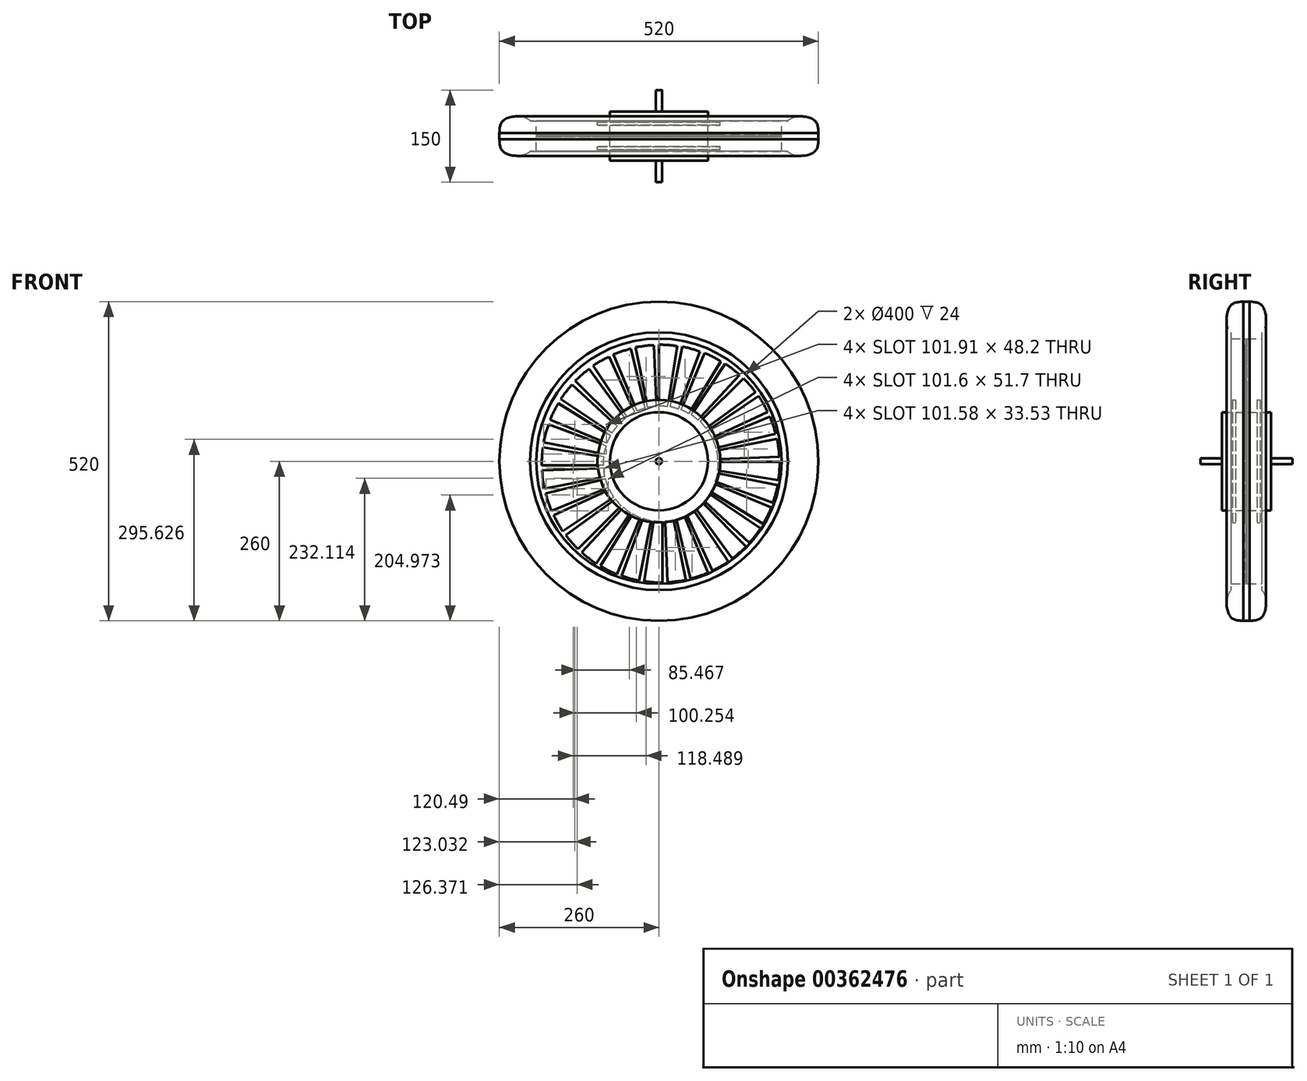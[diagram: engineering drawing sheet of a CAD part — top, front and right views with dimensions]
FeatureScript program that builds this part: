
annotation { "Feature Type Name" : "Feature", "Feature Type Description" : "" }
export const myFeature = defineFeature(function(context is Context, id is Id, definition is map)
    precondition{}
    {
        {
            var Q0;
            Q0=qCreatedBy(makeId("Right.planeOp"),FACE);
            var sketch = newSketch(context, id + "F0", { "sketchPlane" : qUnion([Q0])});
            skLineSegment(sketch, "E0", {"start": v(0, 0) * mm, "end": v(0, 200) * mm, "construction": true});
            skPoint(sketch, "E1.middle", {"position": v(0, 200) * mm});
            skPoint(sketch, "E2.visualSharp", {"position": v(-30.2, 260) * mm});
            skLineSegment(sketch, "E3.left", {"start": v(-1, 200) * mm, "end": v(-1, 80) * mm});
            skLineSegment(sketch, "E4.trimOffspring", {"start": v(-1, 200) * mm, "end": v(-25, 200) * mm});
            skLineSegment(sketch, "E5", {"start": v(-25, 200) * mm, "end": v(-25, 210) * mm});
            skFitSpline(sketch, "E6", {"points": [v(-5, 260) * mm, v(-25.83, 253.38) * mm, v(-32.03, 227.8) * mm, v(-25, 210) * mm], "startDerivative": vector(-86.17, -1.88) * mm, "endDerivative": vector(37.49, -43.12) * mm});
            skLineSegment(sketch, "E7", {"start": v(0, 260) * mm, "end": v(-5, 260) * mm});
            skLineSegment(sketch, "E8", {"start": v(0, 0) * mm, "end": v(-40, 0) * mm});
            skLineSegment(sketch, "E9", {"start": v(-40, 0) * mm, "end": v(-40, 80) * mm});
            skLineSegment(sketch, "E10", {"start": v(-40, 80) * mm, "end": v(-22.5, 80) * mm});
            skLineSegment(sketch, "E11", {"start": v(-22.5, 80) * mm, "end": v(-22.5, 100) * mm});
            skLineSegment(sketch, "E12", {"start": v(-22.5, 100) * mm, "end": v(-17.5, 100) * mm});
            skLineSegment(sketch, "E13", {"start": v(-17.5, 100) * mm, "end": v(-17.5, 80) * mm});
            skLineSegment(sketch, "E14", {"start": v(-17.5, 80) * mm, "end": v(-1, 80) * mm});
            skLineSegment(sketch, "E15.MirrorCS", {"start": v(0, 260) * mm, "end": v(5, 260) * mm});
            skLineSegment(sketch, "E16.MirrorCS", {"start": v(22.5, 100) * mm, "end": v(17.5, 100) * mm});
            skLineSegment(sketch, "E17.MirrorCS", {"start": v(25, 200) * mm, "end": v(25, 210) * mm});
            skLineSegment(sketch, "E18.MirrorCS", {"start": v(1, 200) * mm, "end": v(1, 80) * mm});
            skLineSegment(sketch, "E19.MirrorCS", {"start": v(1, 200) * mm, "end": v(25, 200) * mm});
            skLineSegment(sketch, "E20.MirrorCS", {"start": v(22.5, 80) * mm, "end": v(22.5, 100) * mm});
            skLineSegment(sketch, "E21.MirrorCS", {"start": v(17.5, 100) * mm, "end": v(17.5, 80) * mm});
            skFitSpline(sketch, "E22.MirrorCS", {"points": [v(5, 260) * mm, v(25.83, 253.38) * mm, v(32.03, 227.8) * mm, v(25, 210) * mm], "startDerivative": vector(86.17, -1.88) * mm, "endDerivative": vector(-37.49, -43.12) * mm});
            skLineSegment(sketch, "E23.MirrorCS", {"start": v(40, 80) * mm, "end": v(22.5, 80) * mm});
            skLineSegment(sketch, "E24.MirrorCS", {"start": v(40, 0) * mm, "end": v(40, 80) * mm});
            skLineSegment(sketch, "E25.MirrorCS", {"start": v(0, 0) * mm, "end": v(40, 0) * mm});
            skLineSegment(sketch, "E26.MirrorCS", {"start": v(17.5, 80) * mm, "end": v(1, 80) * mm});
            skPoint(sketch, "E27.MirrorP", {"position": v(30.2, 260) * mm});
            skSolve(sketch);
        }
        {
            var Q0;
            Q0=makeQuery(id+"F0.imprint","IMPRINT",FACE,{"disambiguationData":[TD([[makeQuery(id+"F0.imprint","IMPRINT",EDGE,{"derivedFrom":sQuery(id+"F0.wireOp",EDGE,"E3.left")}),1.0]])]});
            var Q1;
            Q1=sQuery(id+"F0.wireOp",EDGE,"E8");
            revolve(context, id + "F1", {"entities" : qUnion([Q0]), "axis" : qUnion([Q1]), "revolveType" : RevolveType.FULL});
        }
        {
            var Q0;
            Q0=makeQuery(id+"F1.opRevolve","SWEPT_FACE",FACE,{"disambiguationData":[OSD([sQuery(id+"F0.wireOp",EDGE,"E3.left")])]});
            var sketch = newSketch(context, id + "F2", { "sketchPlane" : qUnion([Q0])});
            skLineSegment(sketch, "E28", {"start": v(0, 90) * mm, "end": v(0, 190) * mm});
            skArc(sketch, "E29", {"start": v(0, 90) * mm, "mid": v(7.06, 89.72) * mm, "end": v(14.08, 88.9) * mm});
            skArc(sketch, "E30", {"start": v(0, 190) * mm, "mid": v(14.9, 189.41) * mm, "end": v(29.72, 187.66) * mm});
            skLineSegment(sketch, "E31", {"start": v(14.08, 88.9) * mm, "end": v(29.72, 187.66) * mm});
            skLineSegment(sketch, "E32.1.0", {"start": v(-18.28, 87.63) * mm, "end": v(-37.79, 185.7) * mm});
            skArc(sketch, "E32.1.1", {"start": v(-37.79, 185.7) * mm, "mid": v(-23.05, 188.04) * mm, "end": v(-8.18, 189.21) * mm});
            skLineSegment(sketch, "E32.1.2", {"start": v(-4.25, 89.3) * mm, "end": v(-8.18, 189.21) * mm});
            skArc(sketch, "E32.1.3", {"start": v(-18.28, 87.63) * mm, "mid": v(-11.3, 88.74) * mm, "end": v(-4.25, 89.3) * mm});
            skLineSegment(sketch, "E32.2.0", {"start": v(-35.74, 81.74) * mm, "end": v(-74.01, 174.13) * mm});
            skArc(sketch, "E32.2.1", {"start": v(-74.01, 174.13) * mm, "mid": v(-60.01, 179.3) * mm, "end": v(-45.66, 183.34) * mm});
            skLineSegment(sketch, "E32.2.2", {"start": v(-22.31, 86.1) * mm, "end": v(-45.66, 183.34) * mm});
            skArc(sketch, "E32.2.3", {"start": v(-35.74, 81.74) * mm, "mid": v(-29.11, 84.19) * mm, "end": v(-22.31, 86.1) * mm});
            skPoint(sketch, "E32.center", {"position": v(2.89, -3.98) * mm});
            skLineSegment(sketch, "E33.1.3.0", {"start": v(-51.72, 72.56) * mm, "end": v(-107.28, 155.7) * mm});
            skArc(sketch, "E33.3.3.0", {"start": v(-107.28, 155.7) * mm, "mid": v(-94.56, 163.5) * mm, "end": v(-81.27, 170.27) * mm});
            skLineSegment(sketch, "E33.7.3.0", {"start": v(-39.4, 79.46) * mm, "end": v(-81.27, 170.27) * mm});
            skArc(sketch, "E33.10.3.0", {"start": v(-51.72, 72.56) * mm, "mid": v(-45.7, 76.25) * mm, "end": v(-39.4, 79.46) * mm});
            skLineSegment(sketch, "E33.1.4.0", {"start": v(-65.6, 60.43) * mm, "end": v(-136.32, 131.14) * mm});
            skArc(sketch, "E33.3.4.0", {"start": v(-136.32, 131.14) * mm, "mid": v(-125.36, 141.27) * mm, "end": v(-113.64, 150.5) * mm});
            skLineSegment(sketch, "E33.7.4.0", {"start": v(-54.87, 69.6) * mm, "end": v(-113.64, 150.5) * mm});
            skArc(sketch, "E33.10.4.0", {"start": v(-65.6, 60.43) * mm, "mid": v(-60.42, 65.23) * mm, "end": v(-54.87, 69.6) * mm});
            skLineSegment(sketch, "E33.1.5.0", {"start": v(-76.85, 45.83) * mm, "end": v(-160, 101.39) * mm});
            skArc(sketch, "E33.3.5.0", {"start": v(-160, 101.39) * mm, "mid": v(-151.23, 113.46) * mm, "end": v(-141.54, 124.8) * mm});
            skLineSegment(sketch, "E33.7.5.0", {"start": v(-68.11, 56.92) * mm, "end": v(-141.54, 124.8) * mm});
            skArc(sketch, "E33.10.5.0", {"start": v(-76.85, 45.83) * mm, "mid": v(-72.7, 51.55) * mm, "end": v(-68.11, 56.92) * mm});
            skLineSegment(sketch, "E33.1.6.0", {"start": v(-85.04, 29.32) * mm, "end": v(-177.43, 67.59) * mm});
            skArc(sketch, "E33.3.6.0", {"start": v(-177.43, 67.59) * mm, "mid": v(-171.18, 81.13) * mm, "end": v(-163.9, 94.15) * mm});
            skLineSegment(sketch, "E33.7.6.0", {"start": v(-78.63, 41.9) * mm, "end": v(-163.9, 94.15) * mm});
            skArc(sketch, "E33.10.6.0", {"start": v(-85.04, 29.32) * mm, "mid": v(-82.08, 35.74) * mm, "end": v(-78.63, 41.9) * mm});
            skLineSegment(sketch, "E33.1.7.0", {"start": v(-89.85, 11.52) * mm, "end": v(-187.92, 31.03) * mm});
            skArc(sketch, "E33.3.7.0", {"start": v(-187.92, 31.03) * mm, "mid": v(-184.44, 45.54) * mm, "end": v(-179.83, 59.73) * mm});
            skLineSegment(sketch, "E33.7.7.0", {"start": v(-86.01, 25.12) * mm, "end": v(-179.83, 59.73) * mm});
            skArc(sketch, "E33.10.7.0", {"start": v(-89.85, 11.52) * mm, "mid": v(-88.2, 18.4) * mm, "end": v(-86.01, 25.12) * mm});
            skLineSegment(sketch, "E33.1.8.0", {"start": v(-91.09, -6.87) * mm, "end": v(-191.09, -6.87) * mm});
            skArc(sketch, "E33.3.8.0", {"start": v(-191.09, -6.87) * mm, "mid": v(-190.5, 8.04) * mm, "end": v(-188.75, 22.86) * mm});
            skLineSegment(sketch, "E33.7.8.0", {"start": v(-89.98, 7.21) * mm, "end": v(-188.75, 22.86) * mm});
            skArc(sketch, "E33.10.8.0", {"start": v(-91.09, -6.87) * mm, "mid": v(-90.8, 0.2) * mm, "end": v(-89.98, 7.21) * mm});
            skLineSegment(sketch, "E33.1.9.0", {"start": v(-88.72, -25.14) * mm, "end": v(-186.8, -44.65) * mm});
            skArc(sketch, "E33.3.9.0", {"start": v(-186.8, -44.65) * mm, "mid": v(-189.13, -29.92) * mm, "end": v(-190.3, -15.04) * mm});
            skLineSegment(sketch, "E33.7.9.0", {"start": v(-90.38, -11.12) * mm, "end": v(-190.3, -15.04) * mm});
            skArc(sketch, "E33.10.9.0", {"start": v(-88.72, -25.14) * mm, "mid": v(-89.82, -18.16) * mm, "end": v(-90.38, -11.12) * mm});
            skLineSegment(sketch, "E33.1.10.0", {"start": v(-82.83, -42.6) * mm, "end": v(-175.22, -80.88) * mm});
            skArc(sketch, "E33.3.10.0", {"start": v(-175.22, -80.88) * mm, "mid": v(-180.38, -66.88) * mm, "end": v(-184.43, -52.52) * mm});
            skLineSegment(sketch, "E33.7.10.0", {"start": v(-87.2, -29.18) * mm, "end": v(-184.43, -52.52) * mm});
            skArc(sketch, "E33.10.10.0", {"start": v(-82.83, -42.6) * mm, "mid": v(-85.27, -35.98) * mm, "end": v(-87.2, -29.18) * mm});
            skLineSegment(sketch, "E33.1.11.0", {"start": v(-73.64, -58.59) * mm, "end": v(-156.8, -114.15) * mm});
            skArc(sketch, "E33.3.11.0", {"start": v(-156.8, -114.15) * mm, "mid": v(-164.59, -101.43) * mm, "end": v(-171.36, -88.13) * mm});
            skLineSegment(sketch, "E33.7.11.0", {"start": v(-80.55, -46.27) * mm, "end": v(-171.36, -88.13) * mm});
            skArc(sketch, "E33.10.11.0", {"start": v(-73.64, -58.59) * mm, "mid": v(-77.34, -52.56) * mm, "end": v(-80.55, -46.27) * mm});
            skLineSegment(sketch, "E33.1.12.0", {"start": v(-61.52, -72.47) * mm, "end": v(-132.23, -143.18) * mm});
            skArc(sketch, "E33.3.12.0", {"start": v(-132.23, -143.18) * mm, "mid": v(-142.36, -132.23) * mm, "end": v(-151.6, -120.51) * mm});
            skLineSegment(sketch, "E33.7.12.0", {"start": v(-70.7, -61.73) * mm, "end": v(-151.6, -120.51) * mm});
            skArc(sketch, "E33.10.12.0", {"start": v(-61.52, -72.47) * mm, "mid": v(-66.32, -67.28) * mm, "end": v(-70.7, -61.73) * mm});
            skLineSegment(sketch, "E33.1.13.0", {"start": v(-46.92, -83.72) * mm, "end": v(-102.48, -166.87) * mm});
            skArc(sketch, "E33.3.13.0", {"start": v(-102.48, -166.87) * mm, "mid": v(-114.55, -158.1) * mm, "end": v(-125.9, -148.4) * mm});
            skLineSegment(sketch, "E33.7.13.0", {"start": v(-58.01, -74.98) * mm, "end": v(-125.9, -148.4) * mm});
            skArc(sketch, "E33.10.13.0", {"start": v(-46.92, -83.72) * mm, "mid": v(-52.64, -79.57) * mm, "end": v(-58.01, -74.98) * mm});
            skLineSegment(sketch, "E33.1.14.0", {"start": v(-30.4, -91.9) * mm, "end": v(-68.67, -184.3) * mm});
            skArc(sketch, "E33.3.14.0", {"start": v(-68.67, -184.3) * mm, "mid": v(-82.22, -178.05) * mm, "end": v(-95.24, -170.76) * mm});
            skLineSegment(sketch, "E33.7.14.0", {"start": v(-42.99, -85.5) * mm, "end": v(-95.24, -170.76) * mm});
            skArc(sketch, "E33.10.14.0", {"start": v(-30.4, -91.9) * mm, "mid": v(-36.82, -88.95) * mm, "end": v(-42.99, -85.5) * mm});
            skLineSegment(sketch, "E33.1.15.0", {"start": v(-12.61, -96.71) * mm, "end": v(-32.12, -194.79) * mm});
            skArc(sketch, "E33.3.15.0", {"start": v(-32.12, -194.79) * mm, "mid": v(-46.63, -191.3) * mm, "end": v(-60.82, -186.7) * mm});
            skLineSegment(sketch, "E33.7.15.0", {"start": v(-26.2, -92.88) * mm, "end": v(-60.82, -186.7) * mm});
            skArc(sketch, "E33.10.15.0", {"start": v(-12.61, -96.71) * mm, "mid": v(-19.48, -95.06) * mm, "end": v(-26.2, -92.88) * mm});
            skLineSegment(sketch, "E33.1.16.0", {"start": v(5.78, -97.95) * mm, "end": v(5.78, -197.95) * mm});
            skArc(sketch, "E33.3.16.0", {"start": v(5.78, -197.95) * mm, "mid": v(-9.13, -197.37) * mm, "end": v(-23.94, -195.61) * mm});
            skLineSegment(sketch, "E33.7.16.0", {"start": v(-8.3, -96.84) * mm, "end": v(-23.94, -195.61) * mm});
            skArc(sketch, "E33.10.16.0", {"start": v(5.78, -97.95) * mm, "mid": v(-1.28, -97.68) * mm, "end": v(-8.3, -96.84) * mm});
            skLineSegment(sketch, "E33.1.17.0", {"start": v(24.06, -95.58) * mm, "end": v(43.57, -193.66) * mm});
            skArc(sketch, "E33.3.17.0", {"start": v(43.57, -193.66) * mm, "mid": v(28.83, -196) * mm, "end": v(13.96, -197.17) * mm});
            skLineSegment(sketch, "E33.7.17.0", {"start": v(10.03, -97.24) * mm, "end": v(13.96, -197.17) * mm});
            skArc(sketch, "E33.10.17.0", {"start": v(24.06, -95.58) * mm, "mid": v(17.08, -96.69) * mm, "end": v(10.03, -97.24) * mm});
            skLineSegment(sketch, "E34.1.18.0", {"start": v(41.52, -89.7) * mm, "end": v(79.79, -182.08) * mm});
            skArc(sketch, "E34.3.18.0", {"start": v(79.79, -182.08) * mm, "mid": v(65.8, -187.25) * mm, "end": v(51.43, -191.3) * mm});
            skLineSegment(sketch, "E34.7.18.0", {"start": v(28.09, -94.06) * mm, "end": v(51.43, -191.3) * mm});
            skArc(sketch, "E34.10.18.0", {"start": v(41.52, -89.7) * mm, "mid": v(34.9, -92.14) * mm, "end": v(28.09, -94.06) * mm});
            skLineSegment(sketch, "E34.1.19.0", {"start": v(57.5, -80.5) * mm, "end": v(113.06, -163.66) * mm});
            skArc(sketch, "E34.3.19.0", {"start": v(113.06, -163.66) * mm, "mid": v(100.34, -171.45) * mm, "end": v(87.05, -178.22) * mm});
            skLineSegment(sketch, "E34.7.19.0", {"start": v(45.18, -87.41) * mm, "end": v(87.05, -178.22) * mm});
            skArc(sketch, "E34.10.19.0", {"start": v(57.5, -80.5) * mm, "mid": v(51.48, -84.2) * mm, "end": v(45.18, -87.41) * mm});
            skLineSegment(sketch, "E34.1.20.0", {"start": v(71.38, -68.38) * mm, "end": v(142.1, -139.1) * mm});
            skArc(sketch, "E34.3.20.0", {"start": v(142.1, -139.1) * mm, "mid": v(131.14, -149.22) * mm, "end": v(119.42, -158.46) * mm});
            skLineSegment(sketch, "E34.7.20.0", {"start": v(60.64, -77.56) * mm, "end": v(119.42, -158.46) * mm});
            skArc(sketch, "E34.10.20.0", {"start": v(71.38, -68.38) * mm, "mid": v(66.2, -73.18) * mm, "end": v(60.64, -77.56) * mm});
            skLineSegment(sketch, "E34.1.21.0", {"start": v(82.63, -53.78) * mm, "end": v(165.78, -109.34) * mm});
            skArc(sketch, "E34.3.21.0", {"start": v(165.78, -109.34) * mm, "mid": v(157.01, -121.41) * mm, "end": v(147.32, -132.76) * mm});
            skLineSegment(sketch, "E34.7.21.0", {"start": v(73.89, -64.88) * mm, "end": v(147.32, -132.76) * mm});
            skArc(sketch, "E34.10.21.0", {"start": v(82.63, -53.78) * mm, "mid": v(78.48, -59.5) * mm, "end": v(73.89, -64.88) * mm});
            skLineSegment(sketch, "E34.1.22.0", {"start": v(90.82, -37.27) * mm, "end": v(183.2, -75.54) * mm});
            skArc(sketch, "E34.3.22.0", {"start": v(183.2, -75.54) * mm, "mid": v(176.96, -89.09) * mm, "end": v(169.67, -102.1) * mm});
            skLineSegment(sketch, "E34.7.22.0", {"start": v(84.4, -49.85) * mm, "end": v(169.67, -102.1) * mm});
            skArc(sketch, "E34.10.22.0", {"start": v(90.82, -37.27) * mm, "mid": v(87.86, -43.69) * mm, "end": v(84.4, -49.85) * mm});
            skLineSegment(sketch, "E34.1.23.0", {"start": v(95.62, -19.48) * mm, "end": v(193.7, -38.99) * mm});
            skArc(sketch, "E34.3.23.0", {"start": v(193.7, -38.99) * mm, "mid": v(190.22, -53.5) * mm, "end": v(185.6, -67.68) * mm});
            skLineSegment(sketch, "E34.7.23.0", {"start": v(91.79, -33.07) * mm, "end": v(185.6, -67.68) * mm});
            skArc(sketch, "E34.10.23.0", {"start": v(95.62, -19.48) * mm, "mid": v(93.97, -26.35) * mm, "end": v(91.79, -33.07) * mm});
            skLineSegment(sketch, "E34.1.24.0", {"start": v(96.87, -1.09) * mm, "end": v(196.87, -1.09) * mm});
            skArc(sketch, "E34.3.24.0", {"start": v(196.87, -1.09) * mm, "mid": v(196.28, -16) * mm, "end": v(194.53, -30.8) * mm});
            skLineSegment(sketch, "E34.7.24.0", {"start": v(95.76, -15.17) * mm, "end": v(194.53, -30.8) * mm});
            skArc(sketch, "E34.10.24.0", {"start": v(96.87, -1.09) * mm, "mid": v(96.59, -8.15) * mm, "end": v(95.76, -15.17) * mm});
            skLineSegment(sketch, "E34.1.25.0", {"start": v(94.5, 17.2) * mm, "end": v(192.57, 36.7) * mm});
            skArc(sketch, "E34.3.25.0", {"start": v(192.57, 36.7) * mm, "mid": v(194.9, 21.96) * mm, "end": v(196.08, 7.1) * mm});
            skLineSegment(sketch, "E34.7.25.0", {"start": v(96.16, 3.17) * mm, "end": v(196.08, 7.1) * mm});
            skArc(sketch, "E34.10.25.0", {"start": v(94.5, 17.2) * mm, "mid": v(95.6, 10.21) * mm, "end": v(96.16, 3.17) * mm});
            skLineSegment(sketch, "E34.1.26.0", {"start": v(88.6, 34.66) * mm, "end": v(181, 72.92) * mm});
            skArc(sketch, "E34.3.26.0", {"start": v(181, 72.92) * mm, "mid": v(186.16, 58.93) * mm, "end": v(190.2, 44.57) * mm});
            skLineSegment(sketch, "E34.7.26.0", {"start": v(92.97, 21.22) * mm, "end": v(190.2, 44.57) * mm});
            skArc(sketch, "E34.10.26.0", {"start": v(88.6, 34.66) * mm, "mid": v(91.05, 28.03) * mm, "end": v(92.97, 21.22) * mm});
            skLineSegment(sketch, "E34.1.27.0", {"start": v(79.42, 50.64) * mm, "end": v(162.57, 106.2) * mm});
            skArc(sketch, "E34.3.27.0", {"start": v(162.57, 106.2) * mm, "mid": v(170.36, 93.47) * mm, "end": v(177.14, 80.18) * mm});
            skLineSegment(sketch, "E34.7.27.0", {"start": v(86.32, 38.31) * mm, "end": v(177.14, 80.18) * mm});
            skArc(sketch, "E34.10.27.0", {"start": v(79.42, 50.64) * mm, "mid": v(83.11, 44.61) * mm, "end": v(86.32, 38.31) * mm});
            skLineSegment(sketch, "E34.1.28.0", {"start": v(67.3, 64.52) * mm, "end": v(138, 135.23) * mm});
            skArc(sketch, "E34.3.28.0", {"start": v(138, 135.23) * mm, "mid": v(148.13, 124.27) * mm, "end": v(157.37, 112.56) * mm});
            skLineSegment(sketch, "E34.7.28.0", {"start": v(76.47, 53.78) * mm, "end": v(157.37, 112.56) * mm});
            skArc(sketch, "E34.10.28.0", {"start": v(67.3, 64.52) * mm, "mid": v(72.1, 59.33) * mm, "end": v(76.47, 53.78) * mm});
            skLineSegment(sketch, "E34.1.29.0", {"start": v(52.7, 75.77) * mm, "end": v(108.25, 158.91) * mm});
            skArc(sketch, "E34.3.29.0", {"start": v(108.25, 158.91) * mm, "mid": v(120.32, 150.15) * mm, "end": v(131.67, 140.46) * mm});
            skLineSegment(sketch, "E34.7.29.0", {"start": v(63.79, 67.02) * mm, "end": v(131.67, 140.46) * mm});
            skArc(sketch, "E34.10.29.0", {"start": v(52.7, 75.77) * mm, "mid": v(58.41, 71.61) * mm, "end": v(63.79, 67.02) * mm});
            skLineSegment(sketch, "E34.1.30.0", {"start": v(36.18, 83.95) * mm, "end": v(74.45, 176.34) * mm});
            skArc(sketch, "E34.3.30.0", {"start": v(74.45, 176.34) * mm, "mid": v(88, 170.1) * mm, "end": v(101.02, 162.8) * mm});
            skLineSegment(sketch, "E34.7.30.0", {"start": v(48.77, 77.54) * mm, "end": v(101.02, 162.8) * mm});
            skArc(sketch, "E34.10.30.0", {"start": v(36.18, 83.95) * mm, "mid": v(42.6, 81) * mm, "end": v(48.77, 77.54) * mm});
            skLineSegment(sketch, "E34.1.31.0", {"start": v(18.39, 88.76) * mm, "end": v(37.9, 186.84) * mm});
            skArc(sketch, "E34.3.31.0", {"start": v(37.9, 186.84) * mm, "mid": v(52.4, 183.35) * mm, "end": v(66.6, 178.74) * mm});
            skLineSegment(sketch, "E34.7.31.0", {"start": v(31.98, 84.92) * mm, "end": v(66.6, 178.74) * mm});
            skArc(sketch, "E34.10.31.0", {"start": v(18.39, 88.76) * mm, "mid": v(25.26, 87.1) * mm, "end": v(31.98, 84.92) * mm});
            skSolve(sketch);
        }
        {
            var Q0;
            Q0 = qSketchRegion(id + "F2", true);
            extrude(context, id + "F3", {"entities" : qUnion([Q0]), "operationType" : NewBodyOperationType.REMOVE, "oppositeDirection" : true, "depth" : 10 * mm});
        }
        {
            var Q0;
            Q0=makeQuery(id+"F1.opRevolve","SWEPT_FACE",FACE,{"disambiguationData":[OSD([sQuery(id+"F0.wireOp",EDGE,"E9")])]});
            var sketch = newSketch(context, id + "F4", { "sketchPlane" : qUnion([Q0])});
            skCircle(sketch, "E35", {"center": v(0, 0) * mm, "radius": 5 * mm});
            skSolve(sketch);
        }
        {
            var Q0;
            Q0 = qSketchRegion(id + "F4", true);
            extrude(context, id + "F5", {"entities" : qUnion([Q0]), "operationType" : NewBodyOperationType.ADD, "depth" : 35 * mm, "offsetDistance" : 25 * mm, "hasSecondDirection" : true, "secondDirectionOppositeDirection" : true, "secondDirectionDepth" : 115 * mm});
        }
    });
